FCSTD DOCUMENT  (FreeCAD 0.18R4 (GitTag))
Label: bigcab-shelf_layout
License: All rights reserved
LicenseURL: http://en.wikipedia.org/wiki/All_rights_reserved
objects: Sketcher::SketchObject×1, PartDesign::Body×1
note: 2 computed .brp shape members not serialized (recipe doc carries the construction recipe); baked Part::Feature solids carry a one-line shape summary decoded from their .brp

FEATURE [Sketcher::SketchObject] Sketch
  MapMode = 5
  Support = -> [XY_Plane]
  sketch-geometry (29):
    g0: LineSegment StartX=-304.8 StartY=1066.8 StartZ=0 EndX=304.8 EndY=1066.8 EndZ=0
    g1: LineSegment StartX=304.8 StartY=1066.8 StartZ=0 EndX=304.8 EndY=0 EndZ=0
    g2: LineSegment StartX=304.8 StartY=0 StartZ=0 EndX=-304.8 EndY=0 EndZ=0
    g3: LineSegment StartX=-304.8 StartY=0 StartZ=0 EndX=-304.8 EndY=1066.8 EndZ=0
    g4: LineSegment StartX=-304.8 StartY=533.4 StartZ=0 EndX=304.8 EndY=533.4 EndZ=0
    g5: LineSegment StartX=-304.8 StartY=67.31 StartZ=0 EndX=304.8 EndY=67.31 EndZ=0
    g6: LineSegment StartX=304.8 StartY=67.31 StartZ=0 EndX=304.8 EndY=0 EndZ=0
    g7: LineSegment StartX=304.8 StartY=0 StartZ=0 EndX=-304.8 EndY=0 EndZ=0
    g8: LineSegment StartX=-304.8 StartY=0 StartZ=0 EndX=-304.8 EndY=67.31 EndZ=0
    g9: LineSegment StartX=-304.8 StartY=134.62 StartZ=0 EndX=304.8 EndY=134.62 EndZ=0
    g10: LineSegment StartX=304.8 StartY=134.62 StartZ=0 EndX=304.8 EndY=67.31 EndZ=0
    g11: LineSegment StartX=304.8 StartY=67.31 StartZ=0 EndX=-304.8 EndY=67.31 EndZ=0
    g12: LineSegment StartX=-304.8 StartY=67.31 StartZ=0 EndX=-304.8 EndY=134.62 EndZ=0
    g13: LineSegment StartX=-304.8 StartY=201.93 StartZ=0 EndX=304.8 EndY=201.93 EndZ=0
    g14: LineSegment StartX=304.8 StartY=201.93 StartZ=0 EndX=304.8 EndY=134.62 EndZ=0
    g15: LineSegment StartX=304.8 StartY=134.62 StartZ=0 EndX=-304.8 EndY=134.62 EndZ=0
    g16: LineSegment StartX=-304.8 StartY=134.62 StartZ=0 EndX=-304.8 EndY=201.93 EndZ=0
    g17: LineSegment StartX=-304.8 StartY=269.24 StartZ=0 EndX=304.8 EndY=269.24 EndZ=0
    g18: LineSegment StartX=304.8 StartY=269.24 StartZ=0 EndX=304.8 EndY=201.93 EndZ=0
    g19: LineSegment StartX=304.8 StartY=201.93 StartZ=0 EndX=-304.8 EndY=201.93 EndZ=0
    g20: LineSegment StartX=-304.8 StartY=201.93 StartZ=0 EndX=-304.8 EndY=269.24 EndZ=0
    g21: LineSegment StartX=-304.8 StartY=336.55 StartZ=0 EndX=304.8 EndY=336.55 EndZ=0
    g22: LineSegment StartX=304.8 StartY=336.55 StartZ=0 EndX=304.8 EndY=269.24 EndZ=0
    g23: LineSegment StartX=304.8 StartY=269.24 StartZ=0 EndX=-304.8 EndY=269.24 EndZ=0
    g24: LineSegment StartX=-304.8 StartY=269.24 StartZ=0 EndX=-304.8 EndY=336.55 EndZ=0
    g25: LineSegment StartX=-304.8 StartY=403.86 StartZ=0 EndX=304.8 EndY=403.86 EndZ=0
    g26: LineSegment StartX=304.8 StartY=403.86 StartZ=0 EndX=304.8 EndY=336.55 EndZ=0
    g27: LineSegment StartX=304.8 StartY=336.55 StartZ=0 EndX=-304.8 EndY=336.55 EndZ=0
    g28: LineSegment StartX=-304.8 StartY=336.55 StartZ=0 EndX=-304.8 EndY=403.86 EndZ=0
  constraints (81):
    c: Coincident(g0,g1)
    c: Coincident(g1,g2)
    c: Coincident(g2,g3)
    c: Coincident(g3,g0)
    c: Horizontal(g0)
    c: Vertical(g1)
    c: Vertical(g3)
    c: DistanceY(g1,g1) = 1066.8
    c: DistanceX(g0,g0) = 609.6
    c: PointOnObject(g-1,g2)
    c: Symmetric(g1,g2,g-2)
    c: Horizontal(g4)
    c: PointOnObject(g4,g3)
    c: PointOnObject(g4,g1)
    c: DistanceY(g1,g4) = 533.4
    c: Coincident(g5,g6)
    c: Coincident(g6,g7)
    c: Coincident(g7,g8)
    c: Coincident(g8,g5)
    c: Horizontal(g5)
    c: Horizontal(g7)
    c: Vertical(g6)
    c: Vertical(g8)
    c: PointOnObject(g5,g1)
    c: Coincident(g7,g2)
    c: DistanceY(g2,g5) = 67.31
    c: Coincident(g9,g10)
    c: Coincident(g10,g11)
    c: Coincident(g11,g12)
    c: Coincident(g12,g9)
    c: Horizontal(g9)
    c: Horizontal(g11)
    c: Vertical(g10)
    c: Vertical(g12)
    c: Coincident(g13,g14)
    c: Coincident(g14,g15)
    c: Coincident(g15,g16)
    c: Coincident(g16,g13)
    c: Horizontal(g13)
    c: Horizontal(g15)
    c: Vertical(g14)
    c: Vertical(g16)
    c: Coincident(g17,g18)
    c: Coincident(g18,g19)
    c: Coincident(g19,g20)
    c: Coincident(g20,g17)
    c: Horizontal(g17)
    c: Horizontal(g19)
    c: Vertical(g18)
    c: Vertical(g20)
    c: Coincident(g21,g22)
    c: Coincident(g22,g23)
    c: Coincident(g23,g24)
    c: Coincident(g24,g21)
    c: Horizontal(g21)
    c: Horizontal(g23)
    c: Vertical(g22)
    c: Vertical(g24)
    c: Coincident(g25,g26)
    c: Coincident(g26,g27)
    c: Coincident(g27,g28)
    c: Coincident(g28,g25)
    c: Horizontal(g25)
    c: Horizontal(g27)
    c: Vertical(g26)
    c: Vertical(g28)
    c: Equal(g12,g16)
    c: Equal(g16,g20)
    c: Equal(g20,g24)
    c: Equal(g24,g28)
    c: Coincident(g11,g5)
    c: Coincident(g15,g9)
    c: Coincident(g19,g13)
    c: Coincident(g23,g17)
    c: DistanceY(g28,g28) = 67.31
    c: Coincident(g27,g21)
    c: PointOnObject(g9,g1)
    c: PointOnObject(g13,g1)
    c: PointOnObject(g17,g1)
    c: PointOnObject(g21,g1)
    c: PointOnObject(g25,g1)
FEATURE [PartDesign::Body] Body
  Group = -> [Sketch]
  Origin = -> Origin
